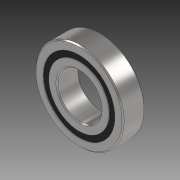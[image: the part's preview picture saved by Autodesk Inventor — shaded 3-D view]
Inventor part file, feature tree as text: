
AUTODESK INVENTOR PART (.ipt)
format: ipt  version: 2020 (Build 240168000, 168)  size: 573,440 bytes
history: mixed  units: in
note: dims shown in document units (in); Inventor stores cm internally (conversion verified against a paired STEP export)
features: other x11, revolve x5, imported_body x1
ambient origin geometry x8: Origin, YZ Plane, XZ Plane, XY Plane, X Axis, Y Axis, Z Axis, Center Point
bodies: Solid1 (imported_parasolid), Solid2 (imported_parasolid), Solid3 (imported_parasolid), Solid4 (imported_parasolid), Solid5 (imported_parasolid), Solid6 (imported_parasolid), Solid7 (imported_parasolid), Solid8 (imported_parasolid), Solid9 (imported_parasolid), Solid10 (imported_parasolid), Solid11 (imported_parasolid), Solid12 (imported_parasolid), Solid13 (imported_parasolid), Solid14 (imported_parasolid), Solid15 (imported_parasolid), Solid16 (imported_parasolid)
feature tree (17):
  revolve  "Revolve1"  [1 undecoded]
  revolve  "Revolve3"  [1 undecoded]
  revolve  "Revolve4"  [1 undecoded]
  other  "CirPattern1[1]"
  other  "CirPattern1[2]"
  other  "CirPattern1[3]"
  other  "CirPattern1[4]"
  other  "CirPattern1[5]"
  other  "CirPattern1[6]"
  other  "CirPattern1[7]"
  other  "CirPattern1[8]"
  other  "CirPattern1[9]"
  other  "CirPattern1[10]"
  other  "CirPattern1[11]"
  revolve  "Revolve5[1]"  [1 undecoded]
  revolve  "Revolve5[2]"  [1 undecoded]
  imported_body  NMx_Import_Brep_tag  [imported B-rep: ~36 faces, bbox_mm=[12.7, 0.0, 12.7]]
note: 5 required parameter values undecoded (feature->parameter linkage not recoverable at this tier; creation-order binding heuristic only, values carry confidence <= 0.55)
